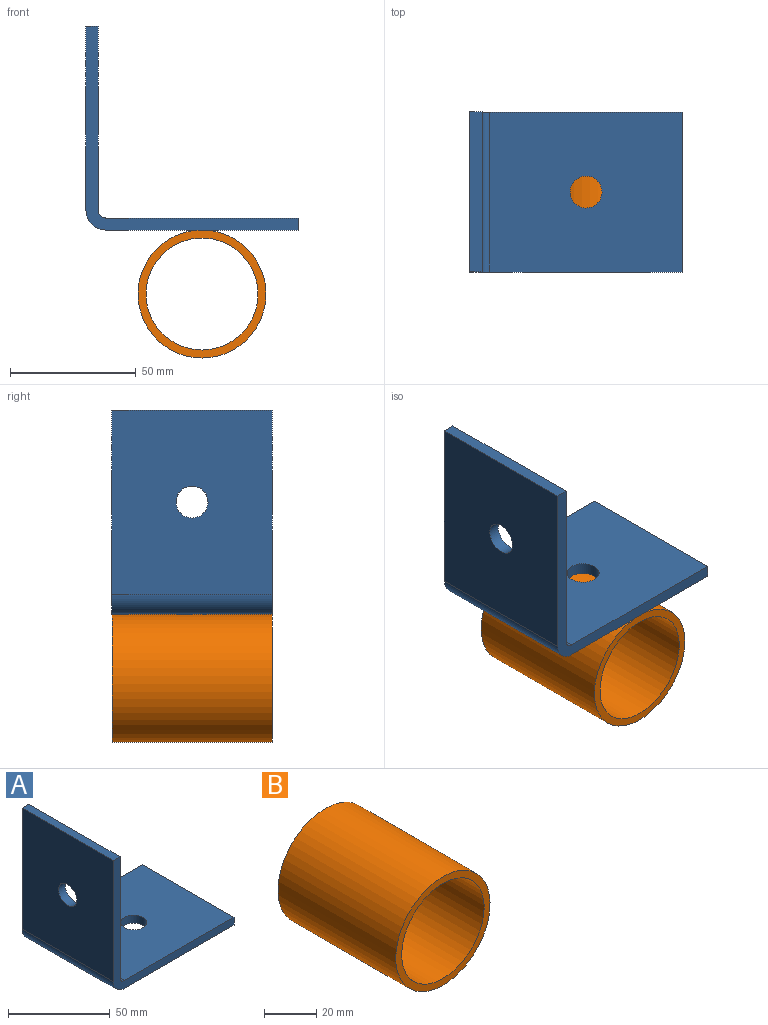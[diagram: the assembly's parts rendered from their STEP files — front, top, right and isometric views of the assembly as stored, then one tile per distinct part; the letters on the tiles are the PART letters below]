
ASSEMBLY  parts=2 mates=1
PART A: 12 faces, bbox 84.1x63.5x81 mm
  f0: plane 73.03x63.5mm, normal (-1,0,0), area 4510.4mm2, adj f1,f7,f8,f9,f11
  f1: cylinder r=7.94mm len=63.5mm, axis (0,1,0), area 791.7mm2, adj f0,f2,f8,f9
  f2: plane 76.2x63.5mm, normal (0,0,-1), area 4712mm2, adj f1,f3,f8,f9,f10
  f3: plane 63.5x4.76mm, normal (1,0,0), area 302.4mm2, adj f2,f4,f8,f9
  f4: plane 76.2x63.5mm, normal (0,0,1), area 4712mm2, adj f3,f5,f8,f9,f10
  f5: cylinder r=3.17mm len=63.5mm, axis (0,1,0), area 316.7mm2, adj f4,f6,f8,f9
  f6: plane 73.03x63.5mm, normal (1,0,0), area 4510.4mm2, adj f5,f7,f8,f9,f11
  f7: plane 63.5x4.76mm, normal (0,0,1), area 302.4mm2, adj f0,f6,f8,f9
  f8: plane 84.14x80.96mm, normal (0,-1,0), area 752.2mm2, adj f0,f1,f2,f3,f4,f5,f6,f7
  f9: plane 84.14x80.96mm, normal (0,1,0), area 752.2mm2, adj f0,f1,f2,f3,f4,f5,f6,f7
  f10: cylinder r=6.35mm len=12.7mm, axis (0,0,1), area 190mm2, adj f2,f4
  f11: cylinder r=6.35mm len=12.7mm, axis (1,0,0), area 190mm2, adj f0,f6
PART B: 4 faces, bbox 50.8x63.5x50.8 mm
  f0: cylinder r=22.23mm len=63.5mm, axis (0,1,0), area 8867.4mm2, adj f2,f3
  f1: cylinder r=25.4mm len=63.5mm, axis (0,1,0), area 10134.1mm2, adj f2,f3
  f2: plane 50.8x50.8mm, normal (0,-1,0), area 475mm2, adj f0,f1
  f3: plane 50.8x50.8mm, normal (0,1,0), area 475mm2, adj f0,f1
PLACE A t=(-41.28,0,30.16)mm
PLACE B at identity fixed
MATE fastened A.f8 <-> B.f2  axis (0,-1,0) through (0,-31.75,25.4)mm
